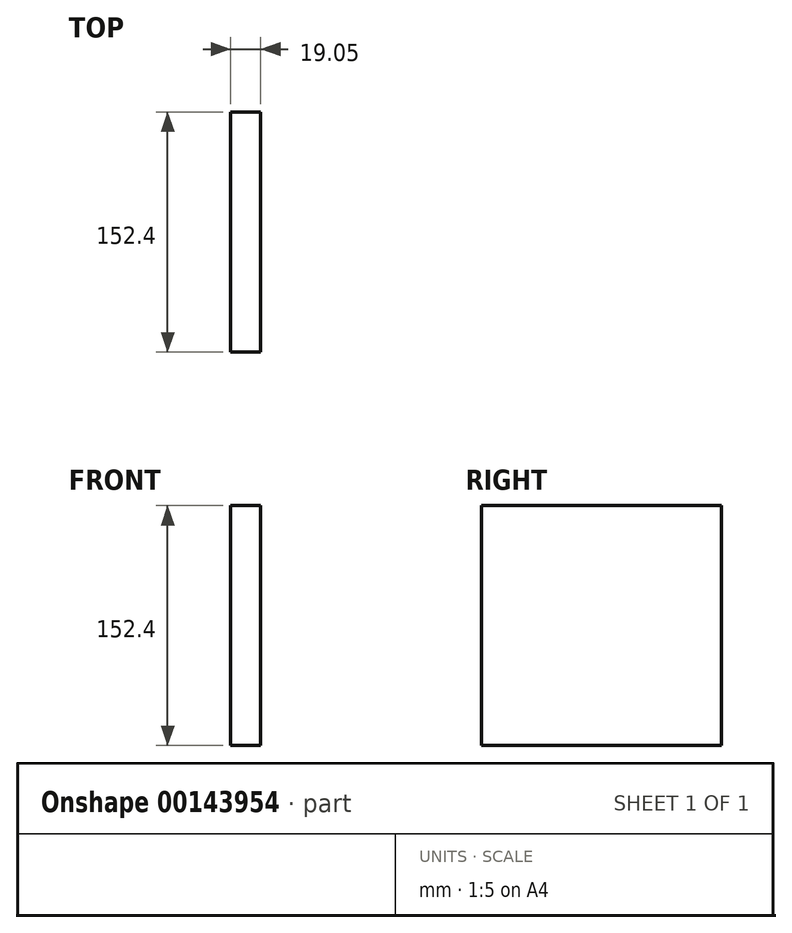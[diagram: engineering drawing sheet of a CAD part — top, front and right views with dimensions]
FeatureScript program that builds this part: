
annotation { "Feature Type Name" : "Feature", "Feature Type Description" : "" }
export const myFeature = defineFeature(function(context is Context, id is Id, definition is map)
    precondition{}
    {
        {
            var Q0;
            Q0=qCreatedBy(makeId("Right.planeOp"),FACE);
            var sketch = newSketch(context, id + "F0", { "sketchPlane" : qUnion([Q0])});
            skLineSegment(sketch, "E0.bottom", {"start": v(-108.34, 36.41) * mm, "end": v(-260.74, 36.41) * mm});
            skLineSegment(sketch, "E0.top", {"start": v(-108.34, -115.99) * mm, "end": v(-260.74, -115.99) * mm});
            skLineSegment(sketch, "E0.left", {"start": v(-108.34, 36.41) * mm, "end": v(-108.34, -115.99) * mm});
            skLineSegment(sketch, "E0.right", {"start": v(-260.74, 36.41) * mm, "end": v(-260.74, -115.99) * mm});
            skSolve(sketch);
        }
        {
            var Q0;
            Q0=makeQuery(id+"F0.imprint","IMPRINT",FACE,{"disambiguationData":[TD([[makeQuery(id+"F0.imprint","IMPRINT",EDGE,{"derivedFrom":sQuery(id+"F0.wireOp",EDGE,"E0.bottom")}),1.0]])]});
            extrude(context, id + "F1", {"entities" : qUnion([Q0]), "depth" : 19.05 * mm});
        }
    });
